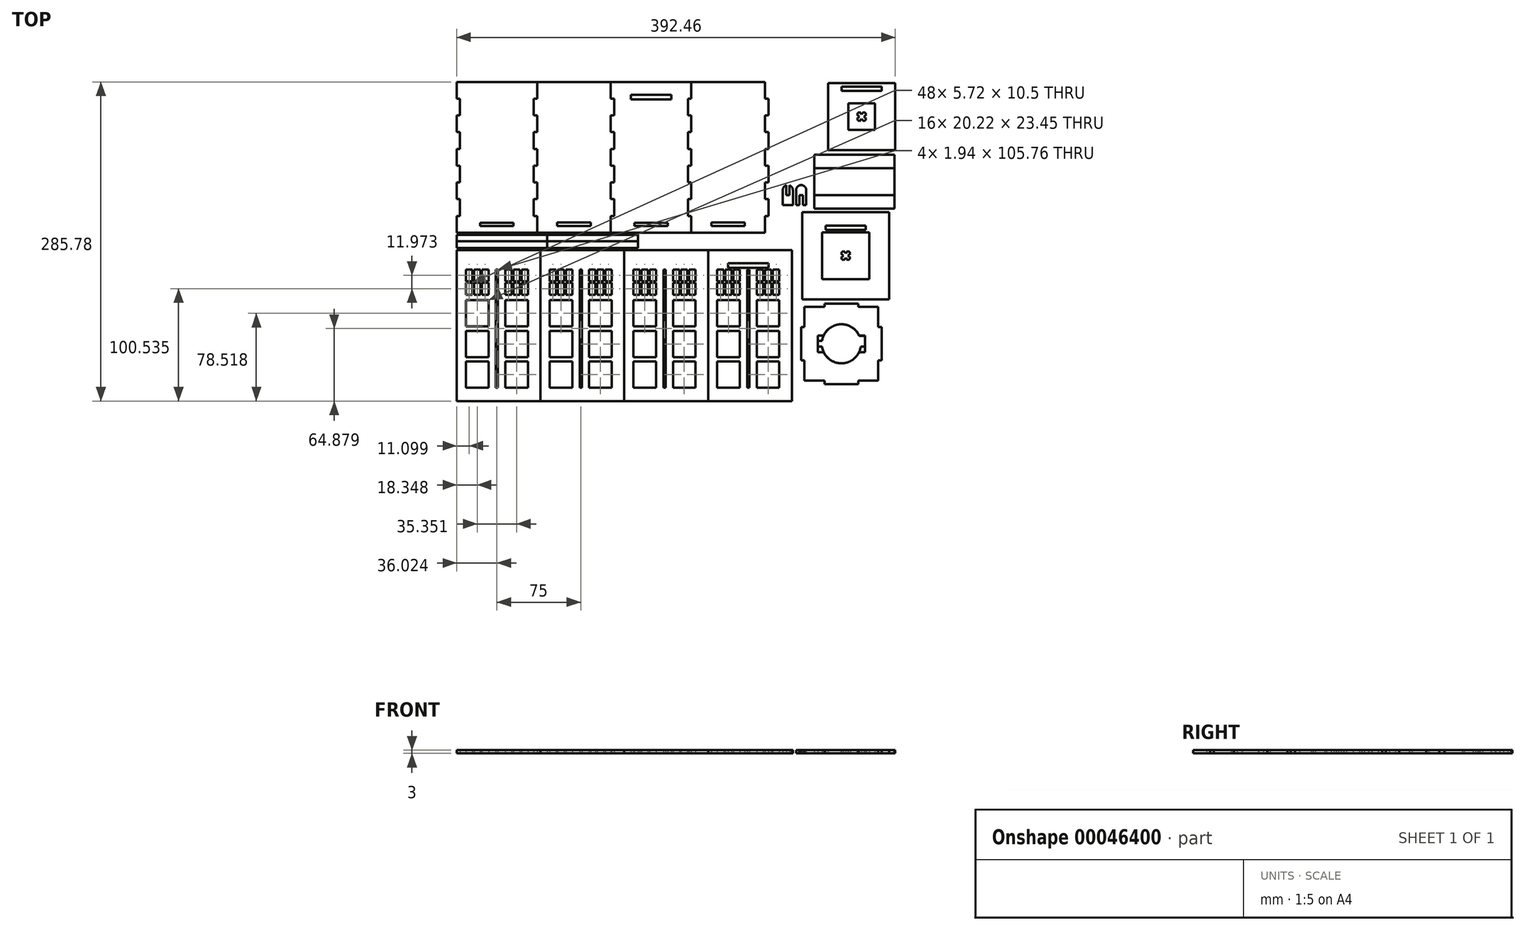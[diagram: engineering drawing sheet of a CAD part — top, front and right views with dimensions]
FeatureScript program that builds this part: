
annotation { "Feature Type Name" : "Feature", "Feature Type Description" : "" }
export const myFeature = defineFeature(function(context is Context, id is Id, definition is map)
    precondition{}
    {
        {
            var Q0;
            Q0=qCreatedBy(makeId("Top.planeOp"),FACE);
            var sketch = newSketch(context, id + "F0", { "sketchPlane" : qUnion([Q0])});
            skLineSegment(sketch, "E0", {"start": v(-210, -148.5) * mm, "end": v(210, -148.5) * mm});
            skLineSegment(sketch, "E1", {"start": v(210, -148.5) * mm, "end": v(210, 148.5) * mm});
            skLineSegment(sketch, "E2", {"start": v(210, 148.5) * mm, "end": v(-210, 148.5) * mm});
            skLineSegment(sketch, "E3", {"start": v(-210, 148.5) * mm, "end": v(-210, -148.5) * mm});
            skArc(sketch, "E4", {"start": v(115.56, 74.24) * mm, "mid": v(115.23, 70.83) * mm, "end": v(114.23, 67.54) * mm});
            skArc(sketch, "E5", {"start": v(114.23, 67.54) * mm, "mid": v(111.59, 63.14) * mm, "end": v(107.78, 59.7) * mm});
            skArc(sketch, "E6", {"start": v(107.78, 59.7) * mm, "mid": v(103.14, 57.5) * mm, "end": v(98.06, 56.74) * mm});
            skArc(sketch, "E7", {"start": v(98.06, 56.74) * mm, "mid": v(94.64, 57.08) * mm, "end": v(91.36, 58.07) * mm});
            skArc(sketch, "E8", {"start": v(91.36, 58.07) * mm, "mid": v(86.96, 60.71) * mm, "end": v(83.5, 64.52) * mm});
            skArc(sketch, "E9", {"start": v(83.5, 64.52) * mm, "mid": v(81.3, 69.16) * mm, "end": v(80.56, 74.24) * mm});
            skArc(sketch, "E10", {"start": v(80.56, 74.24) * mm, "mid": v(80.9, 77.66) * mm, "end": v(81.89, 80.94) * mm});
            skArc(sketch, "E11", {"start": v(81.89, 80.94) * mm, "mid": v(84.53, 85.34) * mm, "end": v(88.33, 88.8) * mm});
            skArc(sketch, "E12", {"start": v(88.33, 88.8) * mm, "mid": v(92.98, 91) * mm, "end": v(98.06, 91.74) * mm});
            skArc(sketch, "E13", {"start": v(98.06, 91.74) * mm, "mid": v(101.47, 91.4) * mm, "end": v(104.76, 90.41) * mm});
            skArc(sketch, "E14", {"start": v(104.76, 90.41) * mm, "mid": v(109.16, 87.77) * mm, "end": v(112.61, 83.97) * mm});
            skArc(sketch, "E15", {"start": v(112.61, 83.97) * mm, "mid": v(114.8, 79.32) * mm, "end": v(115.56, 74.24) * mm});
            skArc(sketch, "E16", {"start": v(127.35, 117.12) * mm, "mid": v(127.24, 114.87) * mm, "end": v(126.92, 112.64) * mm});
            skArc(sketch, "E17", {"start": v(126.92, 112.64) * mm, "mid": v(125.82, 108.84) * mm, "end": v(124.08, 105.3) * mm});
            skArc(sketch, "E18", {"start": v(124.08, 105.3) * mm, "mid": v(120.42, 100.66) * mm, "end": v(115.7, 97.1) * mm});
            skArc(sketch, "E19", {"start": v(115.7, 97.1) * mm, "mid": v(110.22, 94.88) * mm, "end": v(104.35, 94.13) * mm});
            skArc(sketch, "E20", {"start": v(104.35, 94.13) * mm, "mid": v(99.87, 94.56) * mm, "end": v(95.55, 95.87) * mm});
            skArc(sketch, "E21", {"start": v(95.55, 95.87) * mm, "mid": v(92.53, 97.4) * mm, "end": v(89.76, 99.34) * mm});
            skArc(sketch, "E22", {"start": v(89.76, 99.34) * mm, "mid": v(86.22, 102.97) * mm, "end": v(83.56, 107.29) * mm});
            skArc(sketch, "E23", {"start": v(83.56, 107.29) * mm, "mid": v(81.9, 112.08) * mm, "end": v(81.35, 117.12) * mm});
            skArc(sketch, "E24", {"start": v(81.35, 117.12) * mm, "mid": v(81.8, 121.61) * mm, "end": v(83.1, 125.93) * mm});
            skArc(sketch, "E25", {"start": v(83.1, 125.93) * mm, "mid": v(86.57, 131.72) * mm, "end": v(91.57, 136.25) * mm});
            skArc(sketch, "E26", {"start": v(91.57, 136.25) * mm, "mid": v(97.67, 139.14) * mm, "end": v(104.35, 140.12) * mm});
            skArc(sketch, "E27", {"start": v(104.35, 140.12) * mm, "mid": v(106.6, 140.02) * mm, "end": v(108.84, 139.69) * mm});
            skArc(sketch, "E28", {"start": v(108.84, 139.69) * mm, "mid": v(112.63, 138.59) * mm, "end": v(116.18, 136.86) * mm});
            skArc(sketch, "E29", {"start": v(116.18, 136.86) * mm, "mid": v(120.82, 133.19) * mm, "end": v(124.37, 128.46) * mm});
            skArc(sketch, "E30", {"start": v(124.37, 128.46) * mm, "mid": v(126.6, 122.99) * mm, "end": v(127.35, 117.12) * mm});
            skLineSegment(sketch, "E31", {"start": v(175.63, -78.56) * mm, "end": v(175.63, -60.56) * mm});
            skLineSegment(sketch, "E32", {"start": v(175.63, -60.56) * mm, "end": v(157.63, -60.56) * mm});
            skLineSegment(sketch, "E33", {"start": v(157.63, -60.56) * mm, "end": v(157.63, -57.56) * mm});
            skLineSegment(sketch, "E34", {"start": v(157.63, -57.56) * mm, "end": v(127.63, -57.56) * mm});
            skLineSegment(sketch, "E35", {"start": v(127.63, -57.56) * mm, "end": v(127.63, -60.56) * mm});
            skLineSegment(sketch, "E36", {"start": v(127.63, -60.56) * mm, "end": v(109.63, -60.56) * mm});
            skLineSegment(sketch, "E37", {"start": v(109.63, -60.56) * mm, "end": v(109.63, -78.56) * mm});
            skLineSegment(sketch, "E38", {"start": v(109.63, -78.56) * mm, "end": v(106.63, -78.56) * mm});
            skLineSegment(sketch, "E39", {"start": v(106.63, -78.56) * mm, "end": v(106.63, -108.56) * mm});
            skLineSegment(sketch, "E40", {"start": v(106.63, -108.56) * mm, "end": v(109.63, -108.56) * mm});
            skLineSegment(sketch, "E41", {"start": v(109.63, -108.56) * mm, "end": v(109.63, -126.56) * mm});
            skLineSegment(sketch, "E42", {"start": v(109.63, -126.56) * mm, "end": v(127.63, -126.56) * mm});
            skLineSegment(sketch, "E43", {"start": v(127.63, -126.56) * mm, "end": v(127.63, -129.56) * mm});
            skLineSegment(sketch, "E44", {"start": v(127.63, -129.56) * mm, "end": v(157.63, -129.56) * mm});
            skLineSegment(sketch, "E45", {"start": v(157.63, -129.56) * mm, "end": v(157.63, -126.56) * mm});
            skLineSegment(sketch, "E46", {"start": v(157.63, -126.56) * mm, "end": v(175.63, -126.56) * mm});
            skLineSegment(sketch, "E47", {"start": v(175.63, -126.56) * mm, "end": v(175.63, -108.56) * mm});
            skLineSegment(sketch, "E48", {"start": v(175.63, -108.56) * mm, "end": v(178.63, -108.56) * mm});
            skLineSegment(sketch, "E49", {"start": v(178.63, -108.56) * mm, "end": v(178.63, -78.56) * mm});
            skLineSegment(sketch, "E50", {"start": v(178.63, -78.56) * mm, "end": v(175.63, -78.56) * mm});
            skLineSegment(sketch, "E51", {"start": v(96.13, 48.35) * mm, "end": v(96.13, 39.6) * mm});
            skLineSegment(sketch, "E52", {"start": v(96.13, 39.6) * mm, "end": v(93.17, 39.6) * mm});
            skLineSegment(sketch, "E53", {"start": v(93.17, 39.6) * mm, "end": v(93.17, 48.33) * mm});
            skArc(sketch, "E54", {"start": v(93.17, 48.33) * mm, "mid": v(91.96, 47.68) * mm, "end": v(91, 46.7) * mm});
            skArc(sketch, "E55", {"start": v(91, 46.7) * mm, "mid": v(90.38, 45.46) * mm, "end": v(90.17, 44.1) * mm});
            skLineSegment(sketch, "E56", {"start": v(90.17, 44.1) * mm, "end": v(90.17, 30.6) * mm});
            skLineSegment(sketch, "E57", {"start": v(90.17, 30.6) * mm, "end": v(99.17, 30.6) * mm});
            skLineSegment(sketch, "E58", {"start": v(99.17, 30.6) * mm, "end": v(99.17, 44.1) * mm});
            skArc(sketch, "E59", {"start": v(99.17, 44.1) * mm, "mid": v(98.96, 45.47) * mm, "end": v(98.33, 46.7) * mm});
            skArc(sketch, "E60", {"start": v(98.33, 46.7) * mm, "mid": v(97.36, 47.7) * mm, "end": v(96.13, 48.35) * mm});
            skArc(sketch, "E61", {"start": v(106.63, 48.6) * mm, "mid": v(104.91, 48.25) * mm, "end": v(103.45, 47.28) * mm});
            skArc(sketch, "E62", {"start": v(103.45, 47.28) * mm, "mid": v(102.47, 45.82) * mm, "end": v(102.13, 44.1) * mm});
            skLineSegment(sketch, "E63", {"start": v(102.13, 44.1) * mm, "end": v(102.13, 30.6) * mm});
            skLineSegment(sketch, "E64", {"start": v(102.13, 30.6) * mm, "end": v(105.13, 30.6) * mm});
            skLineSegment(sketch, "E65", {"start": v(105.13, 30.6) * mm, "end": v(105.13, 39.6) * mm});
            skLineSegment(sketch, "E66", {"start": v(105.13, 39.6) * mm, "end": v(108.13, 39.6) * mm});
            skLineSegment(sketch, "E67", {"start": v(108.13, 39.6) * mm, "end": v(108.13, 30.6) * mm});
            skLineSegment(sketch, "E68", {"start": v(108.13, 30.6) * mm, "end": v(111.13, 30.6) * mm});
            skLineSegment(sketch, "E69", {"start": v(111.13, 30.6) * mm, "end": v(111.13, 44.1) * mm});
            skArc(sketch, "E70", {"start": v(111.13, 44.1) * mm, "mid": v(110.8, 45.82) * mm, "end": v(109.82, 47.28) * mm});
            skArc(sketch, "E71", {"start": v(109.82, 47.28) * mm, "mid": v(108.36, 48.25) * mm, "end": v(106.63, 48.6) * mm});
            skLineSegment(sketch, "E72", {"start": v(118.32, 63.57) * mm, "end": v(118.32, 75.57) * mm});
            skLineSegment(sketch, "E73", {"start": v(118.32, 75.57) * mm, "end": v(190.28, 75.57) * mm});
            skLineSegment(sketch, "E74", {"start": v(190.28, 75.57) * mm, "end": v(190.28, 63.57) * mm});
            skLineSegment(sketch, "E75", {"start": v(118.32, 51.57) * mm, "end": v(118.32, 63.57) * mm});
            skLineSegment(sketch, "E76", {"start": v(118.32, 63.57) * mm, "end": v(190.28, 63.57) * mm});
            skLineSegment(sketch, "E77", {"start": v(190.28, 63.57) * mm, "end": v(190.28, 51.57) * mm});
            skLineSegment(sketch, "E78", {"start": v(118.32, 39.57) * mm, "end": v(118.32, 51.57) * mm});
            skLineSegment(sketch, "E79", {"start": v(118.32, 51.57) * mm, "end": v(190.28, 51.57) * mm});
            skLineSegment(sketch, "E80", {"start": v(190.28, 51.57) * mm, "end": v(190.28, 39.57) * mm});
            skLineSegment(sketch, "E81", {"start": v(118.32, 27.57) * mm, "end": v(118.32, 39.57) * mm});
            skLineSegment(sketch, "E82", {"start": v(118.32, 39.57) * mm, "end": v(190.28, 39.57) * mm});
            skLineSegment(sketch, "E83", {"start": v(190.28, 39.57) * mm, "end": v(190.28, 27.57) * mm});
            skLineSegment(sketch, "E84", {"start": v(190.28, 27.57) * mm, "end": v(118.32, 27.57) * mm});
            skLineSegment(sketch, "E85", {"start": v(185.47, -53.68) * mm, "end": v(107.47, -53.68) * mm});
            skLineSegment(sketch, "E86", {"start": v(107.47, -53.68) * mm, "end": v(107.47, 24.32) * mm});
            skLineSegment(sketch, "E87", {"start": v(107.47, 24.32) * mm, "end": v(185.47, 24.32) * mm});
            skLineSegment(sketch, "E88", {"start": v(185.47, 24.32) * mm, "end": v(185.47, -53.68) * mm});
            skLineSegment(sketch, "E89", {"start": v(-126.69, -9.83) * mm, "end": v(-201.69, -9.83) * mm});
            skLineSegment(sketch, "E90", {"start": v(-201.69, -9.83) * mm, "end": v(-201.69, -144.83) * mm});
            skLineSegment(sketch, "E91", {"start": v(-201.69, -144.83) * mm, "end": v(-126.69, -144.83) * mm});
            skLineSegment(sketch, "E92", {"start": v(-126.69, -144.83) * mm, "end": v(-126.69, -9.83) * mm});
            skLineSegment(sketch, "E93", {"start": v(-126.69, -144.83) * mm, "end": v(-51.69, -144.83) * mm});
            skLineSegment(sketch, "E94", {"start": v(-51.69, -144.83) * mm, "end": v(-51.69, -144.83) * mm});
            skLineSegment(sketch, "E95", {"start": v(-51.69, -144.83) * mm, "end": v(-51.69, -9.83) * mm});
            skLineSegment(sketch, "E96", {"start": v(-51.69, -9.83) * mm, "end": v(-51.69, -9.83) * mm});
            skLineSegment(sketch, "E97", {"start": v(-51.69, -9.83) * mm, "end": v(-126.69, -9.83) * mm});
            skLineSegment(sketch, "E98", {"start": v(-51.69, -144.83) * mm, "end": v(23.31, -144.83) * mm});
            skLineSegment(sketch, "E99", {"start": v(23.31, -144.83) * mm, "end": v(23.31, -9.83) * mm});
            skLineSegment(sketch, "E100", {"start": v(23.31, -9.83) * mm, "end": v(-51.69, -9.83) * mm});
            skLineSegment(sketch, "E101", {"start": v(23.31, -144.83) * mm, "end": v(98.31, -144.83) * mm});
            skLineSegment(sketch, "E102", {"start": v(98.31, -144.83) * mm, "end": v(98.31, -9.83) * mm});
            skLineSegment(sketch, "E103", {"start": v(98.31, -9.83) * mm, "end": v(23.31, -9.83) * mm});
            skLineSegment(sketch, "E104", {"start": v(190.75, 79.8) * mm, "end": v(130.75, 79.8) * mm});
            skLineSegment(sketch, "E105", {"start": v(130.75, 79.8) * mm, "end": v(130.75, 139.8) * mm});
            skLineSegment(sketch, "E106", {"start": v(130.75, 139.8) * mm, "end": v(190.75, 139.8) * mm});
            skLineSegment(sketch, "E107", {"start": v(190.75, 139.8) * mm, "end": v(190.75, 79.8) * mm});
            skLineSegment(sketch, "E108", {"start": v(-39.56, -7.73) * mm, "end": v(-39.56, -1.8) * mm});
            skLineSegment(sketch, "E109", {"start": v(-39.56, -1.8) * mm, "end": v(-39.56, 4.12) * mm});
            skLineSegment(sketch, "E110", {"start": v(-39.56, 4.12) * mm, "end": v(-120.56, 4.12) * mm});
            skLineSegment(sketch, "E111", {"start": v(-120.56, 4.12) * mm, "end": v(-201.56, 4.12) * mm});
            skLineSegment(sketch, "E112", {"start": v(-201.56, 4.12) * mm, "end": v(-201.56, -1.8) * mm});
            skLineSegment(sketch, "E113", {"start": v(-201.56, -1.8) * mm, "end": v(-201.56, -7.73) * mm});
            skLineSegment(sketch, "E114", {"start": v(-201.56, -7.73) * mm, "end": v(-120.56, -7.73) * mm});
            skLineSegment(sketch, "E115", {"start": v(-120.56, -7.73) * mm, "end": v(-39.56, -7.73) * mm});
            skLineSegment(sketch, "E116", {"start": v(74.29, 5.95) * mm, "end": v(74.29, 20.95) * mm});
            skLineSegment(sketch, "E117", {"start": v(74.29, 20.95) * mm, "end": v(77.29, 20.95) * mm});
            skLineSegment(sketch, "E118", {"start": v(77.29, 20.95) * mm, "end": v(77.29, 35.95) * mm});
            skLineSegment(sketch, "E119", {"start": v(77.29, 35.95) * mm, "end": v(74.29, 35.95) * mm});
            skLineSegment(sketch, "E120", {"start": v(74.29, 35.95) * mm, "end": v(74.29, 50.95) * mm});
            skLineSegment(sketch, "E121", {"start": v(74.29, 50.95) * mm, "end": v(77.29, 50.95) * mm});
            skLineSegment(sketch, "E122", {"start": v(77.29, 50.95) * mm, "end": v(77.29, 65.95) * mm});
            skLineSegment(sketch, "E123", {"start": v(77.29, 65.95) * mm, "end": v(74.29, 65.95) * mm});
            skLineSegment(sketch, "E124", {"start": v(74.29, 65.95) * mm, "end": v(74.29, 80.95) * mm});
            skLineSegment(sketch, "E125", {"start": v(74.29, 80.95) * mm, "end": v(77.29, 80.95) * mm});
            skLineSegment(sketch, "E126", {"start": v(77.29, 80.95) * mm, "end": v(77.29, 95.95) * mm});
            skLineSegment(sketch, "E127", {"start": v(77.29, 95.95) * mm, "end": v(74.29, 95.95) * mm});
            skLineSegment(sketch, "E128", {"start": v(74.29, 95.95) * mm, "end": v(74.29, 110.95) * mm});
            skLineSegment(sketch, "E129", {"start": v(74.29, 110.95) * mm, "end": v(77.29, 110.95) * mm});
            skLineSegment(sketch, "E130", {"start": v(77.29, 110.95) * mm, "end": v(77.29, 125.95) * mm});
            skLineSegment(sketch, "E131", {"start": v(77.29, 125.95) * mm, "end": v(74.29, 125.95) * mm});
            skLineSegment(sketch, "E132", {"start": v(74.29, 125.95) * mm, "end": v(74.29, 140.95) * mm});
            skLineSegment(sketch, "E133", {"start": v(74.29, 140.95) * mm, "end": v(-201.71, 140.95) * mm});
            skLineSegment(sketch, "E134", {"start": v(-201.71, 140.95) * mm, "end": v(-201.71, 125.95) * mm});
            skLineSegment(sketch, "E135", {"start": v(-201.71, 125.95) * mm, "end": v(-198.71, 125.95) * mm});
            skLineSegment(sketch, "E136", {"start": v(-198.71, 125.95) * mm, "end": v(-198.71, 110.95) * mm});
            skLineSegment(sketch, "E137", {"start": v(-198.71, 110.95) * mm, "end": v(-201.71, 110.95) * mm});
            skLineSegment(sketch, "E138", {"start": v(-201.71, 110.95) * mm, "end": v(-201.71, 95.95) * mm});
            skLineSegment(sketch, "E139", {"start": v(-201.71, 95.95) * mm, "end": v(-198.71, 95.95) * mm});
            skLineSegment(sketch, "E140", {"start": v(-198.71, 95.95) * mm, "end": v(-198.71, 80.95) * mm});
            skLineSegment(sketch, "E141", {"start": v(-198.71, 80.95) * mm, "end": v(-201.71, 80.95) * mm});
            skLineSegment(sketch, "E142", {"start": v(-201.71, 80.95) * mm, "end": v(-201.71, 65.95) * mm});
            skLineSegment(sketch, "E143", {"start": v(-201.71, 65.95) * mm, "end": v(-198.71, 65.95) * mm});
            skLineSegment(sketch, "E144", {"start": v(-198.71, 65.95) * mm, "end": v(-198.71, 50.95) * mm});
            skLineSegment(sketch, "E145", {"start": v(-198.71, 50.95) * mm, "end": v(-201.71, 50.95) * mm});
            skLineSegment(sketch, "E146", {"start": v(-201.71, 50.95) * mm, "end": v(-201.71, 35.95) * mm});
            skLineSegment(sketch, "E147", {"start": v(-201.71, 35.95) * mm, "end": v(-198.71, 35.95) * mm});
            skLineSegment(sketch, "E148", {"start": v(-198.71, 35.95) * mm, "end": v(-198.71, 20.95) * mm});
            skLineSegment(sketch, "E149", {"start": v(-198.71, 20.95) * mm, "end": v(-201.71, 20.95) * mm});
            skLineSegment(sketch, "E150", {"start": v(-201.71, 20.95) * mm, "end": v(-201.71, 5.95) * mm});
            skLineSegment(sketch, "E151", {"start": v(-201.71, 5.95) * mm, "end": v(74.29, 5.95) * mm});
            skLineSegment(sketch, "E152", {"start": v(-180.71, 11.95) * mm, "end": v(-180.71, 14.68) * mm});
            skLineSegment(sketch, "E153", {"start": v(-180.71, 14.68) * mm, "end": v(-150.71, 14.68) * mm});
            skLineSegment(sketch, "E154", {"start": v(-150.71, 14.68) * mm, "end": v(-150.71, 11.95) * mm});
            skLineSegment(sketch, "E155", {"start": v(-150.71, 11.95) * mm, "end": v(-180.71, 11.95) * mm});
            skLineSegment(sketch, "E156", {"start": v(-111.71, 11.95) * mm, "end": v(-111.71, 14.95) * mm});
            skLineSegment(sketch, "E157", {"start": v(-111.71, 14.95) * mm, "end": v(-81.71, 14.95) * mm});
            skLineSegment(sketch, "E158", {"start": v(-81.71, 14.95) * mm, "end": v(-81.71, 11.95) * mm});
            skLineSegment(sketch, "E159", {"start": v(-81.71, 11.95) * mm, "end": v(-111.71, 11.95) * mm});
            skLineSegment(sketch, "E160", {"start": v(-42.71, 11.95) * mm, "end": v(-42.71, 14.68) * mm});
            skLineSegment(sketch, "E161", {"start": v(-42.71, 14.68) * mm, "end": v(-12.71, 14.68) * mm});
            skLineSegment(sketch, "E162", {"start": v(-12.71, 14.68) * mm, "end": v(-12.71, 11.95) * mm});
            skLineSegment(sketch, "E163", {"start": v(-12.71, 11.95) * mm, "end": v(-42.71, 11.95) * mm});
            skLineSegment(sketch, "E164", {"start": v(26.29, 11.95) * mm, "end": v(26.29, 14.95) * mm});
            skLineSegment(sketch, "E165", {"start": v(26.29, 14.95) * mm, "end": v(56.29, 14.95) * mm});
            skLineSegment(sketch, "E166", {"start": v(56.29, 14.95) * mm, "end": v(56.29, 11.95) * mm});
            skLineSegment(sketch, "E167", {"start": v(56.29, 11.95) * mm, "end": v(26.29, 11.95) * mm});
            skLineSegment(sketch, "E168", {"start": v(-9.71, 125.3) * mm, "end": v(-45.71, 125.3) * mm});
            skLineSegment(sketch, "E169", {"start": v(-45.71, 125.3) * mm, "end": v(-45.71, 129.3) * mm});
            skLineSegment(sketch, "E170", {"start": v(-45.71, 129.3) * mm, "end": v(-9.71, 129.3) * mm});
            skLineSegment(sketch, "E171", {"start": v(-9.71, 129.3) * mm, "end": v(-9.71, 125.3) * mm});
            skLineSegment(sketch, "E172", {"start": v(-37.75, -37.57) * mm, "end": v(-43.47, -37.57) * mm});
            skLineSegment(sketch, "E173", {"start": v(-43.47, -37.57) * mm, "end": v(-43.47, -27.07) * mm});
            skLineSegment(sketch, "E174", {"start": v(-43.47, -27.07) * mm, "end": v(-37.75, -27.07) * mm});
            skLineSegment(sketch, "E175", {"start": v(-37.75, -27.07) * mm, "end": v(-37.75, -37.57) * mm});
            skLineSegment(sketch, "E176", {"start": v(-30.5, -37.57) * mm, "end": v(-36.22, -37.57) * mm});
            skLineSegment(sketch, "E177", {"start": v(-36.22, -37.57) * mm, "end": v(-36.22, -27.07) * mm});
            skLineSegment(sketch, "E178", {"start": v(-36.22, -27.07) * mm, "end": v(-30.5, -27.07) * mm});
            skLineSegment(sketch, "E179", {"start": v(-30.5, -27.07) * mm, "end": v(-30.5, -37.57) * mm});
            skLineSegment(sketch, "E180", {"start": v(-23.26, -37.57) * mm, "end": v(-28.97, -37.57) * mm});
            skLineSegment(sketch, "E181", {"start": v(-28.97, -37.57) * mm, "end": v(-28.97, -27.07) * mm});
            skLineSegment(sketch, "E182", {"start": v(-28.97, -27.07) * mm, "end": v(-23.26, -27.07) * mm});
            skLineSegment(sketch, "E183", {"start": v(-23.26, -27.07) * mm, "end": v(-23.26, -37.57) * mm});
            skLineSegment(sketch, "E184", {"start": v(-37.75, -49.55) * mm, "end": v(-43.47, -49.55) * mm});
            skLineSegment(sketch, "E185", {"start": v(-43.47, -49.55) * mm, "end": v(-43.47, -39.04) * mm});
            skLineSegment(sketch, "E186", {"start": v(-43.47, -39.04) * mm, "end": v(-37.75, -39.04) * mm});
            skLineSegment(sketch, "E187", {"start": v(-37.75, -39.04) * mm, "end": v(-37.75, -49.55) * mm});
            skLineSegment(sketch, "E188", {"start": v(-30.5, -49.55) * mm, "end": v(-36.22, -49.55) * mm});
            skLineSegment(sketch, "E189", {"start": v(-36.22, -49.55) * mm, "end": v(-36.22, -39.04) * mm});
            skLineSegment(sketch, "E190", {"start": v(-36.22, -39.04) * mm, "end": v(-30.5, -39.04) * mm});
            skLineSegment(sketch, "E191", {"start": v(-30.5, -39.04) * mm, "end": v(-30.5, -49.55) * mm});
            skLineSegment(sketch, "E192", {"start": v(-23.26, -49.55) * mm, "end": v(-28.97, -49.55) * mm});
            skLineSegment(sketch, "E193", {"start": v(-28.97, -49.55) * mm, "end": v(-28.97, -39.04) * mm});
            skLineSegment(sketch, "E194", {"start": v(-28.97, -39.04) * mm, "end": v(-23.26, -39.04) * mm});
            skLineSegment(sketch, "E195", {"start": v(-23.26, -39.04) * mm, "end": v(-23.26, -49.55) * mm});
            skLineSegment(sketch, "E196", {"start": v(-23.26, -105.44) * mm, "end": v(-43.47, -105.44) * mm});
            skLineSegment(sketch, "E197", {"start": v(-43.47, -105.44) * mm, "end": v(-43.47, -81.98) * mm});
            skLineSegment(sketch, "E198", {"start": v(-43.47, -81.98) * mm, "end": v(-23.26, -81.98) * mm});
            skLineSegment(sketch, "E199", {"start": v(-23.26, -81.98) * mm, "end": v(-23.26, -105.44) * mm});
            skLineSegment(sketch, "E200", {"start": v(-23.26, -132.83) * mm, "end": v(-43.47, -132.83) * mm});
            skLineSegment(sketch, "E201", {"start": v(-43.47, -132.83) * mm, "end": v(-43.47, -109.38) * mm});
            skLineSegment(sketch, "E202", {"start": v(-43.47, -109.38) * mm, "end": v(-23.26, -109.38) * mm});
            skLineSegment(sketch, "E203", {"start": v(-23.26, -109.38) * mm, "end": v(-23.26, -132.83) * mm});
            skLineSegment(sketch, "E204", {"start": v(6.38, -37.57) * mm, "end": v(12.1, -37.57) * mm});
            skLineSegment(sketch, "E205", {"start": v(12.1, -37.57) * mm, "end": v(12.1, -27.07) * mm});
            skLineSegment(sketch, "E206", {"start": v(12.1, -27.07) * mm, "end": v(6.38, -27.07) * mm});
            skLineSegment(sketch, "E207", {"start": v(6.38, -27.07) * mm, "end": v(6.38, -37.57) * mm});
            skLineSegment(sketch, "E208", {"start": v(-0.87, -37.57) * mm, "end": v(4.85, -37.57) * mm});
            skLineSegment(sketch, "E209", {"start": v(4.85, -37.57) * mm, "end": v(4.85, -27.07) * mm});
            skLineSegment(sketch, "E210", {"start": v(4.85, -27.07) * mm, "end": v(-0.87, -27.07) * mm});
            skLineSegment(sketch, "E211", {"start": v(-0.87, -27.07) * mm, "end": v(-0.87, -37.57) * mm});
            skLineSegment(sketch, "E212", {"start": v(-8.12, -37.57) * mm, "end": v(-2.4, -37.57) * mm});
            skLineSegment(sketch, "E213", {"start": v(-2.4, -37.57) * mm, "end": v(-2.4, -27.07) * mm});
            skLineSegment(sketch, "E214", {"start": v(-2.4, -27.07) * mm, "end": v(-8.12, -27.07) * mm});
            skLineSegment(sketch, "E215", {"start": v(-8.12, -27.07) * mm, "end": v(-8.12, -37.57) * mm});
            skLineSegment(sketch, "E216", {"start": v(6.38, -49.55) * mm, "end": v(12.1, -49.55) * mm});
            skLineSegment(sketch, "E217", {"start": v(12.1, -49.55) * mm, "end": v(12.1, -39.04) * mm});
            skLineSegment(sketch, "E218", {"start": v(12.1, -39.04) * mm, "end": v(6.38, -39.04) * mm});
            skLineSegment(sketch, "E219", {"start": v(6.38, -39.04) * mm, "end": v(6.38, -49.55) * mm});
            skLineSegment(sketch, "E220", {"start": v(-0.87, -49.55) * mm, "end": v(4.85, -49.55) * mm});
            skLineSegment(sketch, "E221", {"start": v(4.85, -49.55) * mm, "end": v(4.85, -39.04) * mm});
            skLineSegment(sketch, "E222", {"start": v(4.85, -39.04) * mm, "end": v(-0.87, -39.04) * mm});
            skLineSegment(sketch, "E223", {"start": v(-0.87, -39.04) * mm, "end": v(-0.87, -49.55) * mm});
            skLineSegment(sketch, "E224", {"start": v(-8.12, -49.55) * mm, "end": v(-2.4, -49.55) * mm});
            skLineSegment(sketch, "E225", {"start": v(-2.4, -49.55) * mm, "end": v(-2.4, -39.04) * mm});
            skLineSegment(sketch, "E226", {"start": v(-2.4, -39.04) * mm, "end": v(-8.12, -39.04) * mm});
            skLineSegment(sketch, "E227", {"start": v(-8.12, -39.04) * mm, "end": v(-8.12, -49.55) * mm});
            skLineSegment(sketch, "E228", {"start": v(-8.12, -105.44) * mm, "end": v(12.1, -105.44) * mm});
            skLineSegment(sketch, "E229", {"start": v(12.1, -105.44) * mm, "end": v(12.1, -81.98) * mm});
            skLineSegment(sketch, "E230", {"start": v(12.1, -81.98) * mm, "end": v(-8.12, -81.98) * mm});
            skLineSegment(sketch, "E231", {"start": v(-8.12, -81.98) * mm, "end": v(-8.12, -105.44) * mm});
            skLineSegment(sketch, "E232", {"start": v(-8.12, -132.83) * mm, "end": v(12.1, -132.83) * mm});
            skLineSegment(sketch, "E233", {"start": v(12.1, -132.83) * mm, "end": v(12.1, -109.38) * mm});
            skLineSegment(sketch, "E234", {"start": v(12.1, -109.38) * mm, "end": v(-8.12, -109.38) * mm});
            skLineSegment(sketch, "E235", {"start": v(-8.12, -109.38) * mm, "end": v(-8.12, -132.83) * mm});
            skLineSegment(sketch, "E236", {"start": v(-8.12, -78.04) * mm, "end": v(12.1, -78.04) * mm});
            skLineSegment(sketch, "E237", {"start": v(12.1, -78.04) * mm, "end": v(12.1, -54.59) * mm});
            skLineSegment(sketch, "E238", {"start": v(12.1, -54.59) * mm, "end": v(-8.12, -54.59) * mm});
            skLineSegment(sketch, "E239", {"start": v(-8.12, -54.59) * mm, "end": v(-8.12, -78.04) * mm});
            skLineSegment(sketch, "E240", {"start": v(-14.71, -132.83) * mm, "end": v(-16.66, -132.83) * mm});
            skLineSegment(sketch, "E241", {"start": v(-16.66, -132.83) * mm, "end": v(-16.66, -27.07) * mm});
            skLineSegment(sketch, "E242", {"start": v(-16.66, -27.07) * mm, "end": v(-14.71, -27.07) * mm});
            skLineSegment(sketch, "E243", {"start": v(-14.71, -27.07) * mm, "end": v(-14.71, -132.83) * mm});
            skLineSegment(sketch, "E244", {"start": v(-43.47, -78.04) * mm, "end": v(-23.25, -78.04) * mm});
            skLineSegment(sketch, "E245", {"start": v(-23.25, -78.04) * mm, "end": v(-23.25, -54.59) * mm});
            skLineSegment(sketch, "E246", {"start": v(-23.25, -54.59) * mm, "end": v(-43.47, -54.59) * mm});
            skLineSegment(sketch, "E247", {"start": v(-43.47, -54.59) * mm, "end": v(-43.47, -78.04) * mm});
            skLineSegment(sketch, "E248", {"start": v(-187.75, -37.57) * mm, "end": v(-193.47, -37.57) * mm});
            skLineSegment(sketch, "E249", {"start": v(-193.47, -37.57) * mm, "end": v(-193.47, -27.07) * mm});
            skLineSegment(sketch, "E250", {"start": v(-193.47, -27.07) * mm, "end": v(-187.75, -27.07) * mm});
            skLineSegment(sketch, "E251", {"start": v(-187.75, -27.07) * mm, "end": v(-187.75, -37.57) * mm});
            skLineSegment(sketch, "E252", {"start": v(-180.5, -37.57) * mm, "end": v(-186.22, -37.57) * mm});
            skLineSegment(sketch, "E253", {"start": v(-186.22, -37.57) * mm, "end": v(-186.22, -27.07) * mm});
            skLineSegment(sketch, "E254", {"start": v(-186.22, -27.07) * mm, "end": v(-180.5, -27.07) * mm});
            skLineSegment(sketch, "E255", {"start": v(-180.5, -27.07) * mm, "end": v(-180.5, -37.57) * mm});
            skLineSegment(sketch, "E256", {"start": v(-173.26, -37.57) * mm, "end": v(-178.97, -37.57) * mm});
            skLineSegment(sketch, "E257", {"start": v(-178.97, -37.57) * mm, "end": v(-178.97, -27.07) * mm});
            skLineSegment(sketch, "E258", {"start": v(-178.97, -27.07) * mm, "end": v(-173.26, -27.07) * mm});
            skLineSegment(sketch, "E259", {"start": v(-173.26, -27.07) * mm, "end": v(-173.26, -37.57) * mm});
            skLineSegment(sketch, "E260", {"start": v(-187.75, -49.55) * mm, "end": v(-193.47, -49.55) * mm});
            skLineSegment(sketch, "E261", {"start": v(-193.47, -49.55) * mm, "end": v(-193.47, -39.04) * mm});
            skLineSegment(sketch, "E262", {"start": v(-193.47, -39.04) * mm, "end": v(-187.75, -39.04) * mm});
            skLineSegment(sketch, "E263", {"start": v(-187.75, -39.04) * mm, "end": v(-187.75, -49.55) * mm});
            skLineSegment(sketch, "E264", {"start": v(-180.5, -49.55) * mm, "end": v(-186.22, -49.55) * mm});
            skLineSegment(sketch, "E265", {"start": v(-186.22, -49.55) * mm, "end": v(-186.22, -39.04) * mm});
            skLineSegment(sketch, "E266", {"start": v(-186.22, -39.04) * mm, "end": v(-180.5, -39.04) * mm});
            skLineSegment(sketch, "E267", {"start": v(-180.5, -39.04) * mm, "end": v(-180.5, -49.55) * mm});
            skLineSegment(sketch, "E268", {"start": v(-173.26, -49.55) * mm, "end": v(-178.97, -49.55) * mm});
            skLineSegment(sketch, "E269", {"start": v(-178.97, -49.55) * mm, "end": v(-178.97, -39.04) * mm});
            skLineSegment(sketch, "E270", {"start": v(-178.97, -39.04) * mm, "end": v(-173.26, -39.04) * mm});
            skLineSegment(sketch, "E271", {"start": v(-173.26, -39.04) * mm, "end": v(-173.26, -49.55) * mm});
            skLineSegment(sketch, "E272", {"start": v(-173.26, -105.44) * mm, "end": v(-193.47, -105.44) * mm});
            skLineSegment(sketch, "E273", {"start": v(-193.47, -105.44) * mm, "end": v(-193.47, -81.98) * mm});
            skLineSegment(sketch, "E274", {"start": v(-193.47, -81.98) * mm, "end": v(-173.26, -81.98) * mm});
            skLineSegment(sketch, "E275", {"start": v(-173.26, -81.98) * mm, "end": v(-173.26, -105.44) * mm});
            skLineSegment(sketch, "E276", {"start": v(-173.26, -132.83) * mm, "end": v(-193.47, -132.83) * mm});
            skLineSegment(sketch, "E277", {"start": v(-193.47, -132.83) * mm, "end": v(-193.47, -109.38) * mm});
            skLineSegment(sketch, "E278", {"start": v(-193.47, -109.38) * mm, "end": v(-173.26, -109.38) * mm});
            skLineSegment(sketch, "E279", {"start": v(-173.26, -109.38) * mm, "end": v(-173.26, -132.83) * mm});
            skLineSegment(sketch, "E280", {"start": v(-143.62, -37.57) * mm, "end": v(-137.9, -37.57) * mm});
            skLineSegment(sketch, "E281", {"start": v(-137.9, -37.57) * mm, "end": v(-137.9, -27.07) * mm});
            skLineSegment(sketch, "E282", {"start": v(-137.9, -27.07) * mm, "end": v(-143.62, -27.07) * mm});
            skLineSegment(sketch, "E283", {"start": v(-143.62, -27.07) * mm, "end": v(-143.62, -37.57) * mm});
            skLineSegment(sketch, "E284", {"start": v(-150.87, -37.57) * mm, "end": v(-145.15, -37.57) * mm});
            skLineSegment(sketch, "E285", {"start": v(-145.15, -37.57) * mm, "end": v(-145.15, -27.07) * mm});
            skLineSegment(sketch, "E286", {"start": v(-145.15, -27.07) * mm, "end": v(-150.87, -27.07) * mm});
            skLineSegment(sketch, "E287", {"start": v(-150.87, -27.07) * mm, "end": v(-150.87, -37.57) * mm});
            skLineSegment(sketch, "E288", {"start": v(-158.12, -37.57) * mm, "end": v(-152.4, -37.57) * mm});
            skLineSegment(sketch, "E289", {"start": v(-152.4, -37.57) * mm, "end": v(-152.4, -27.07) * mm});
            skLineSegment(sketch, "E290", {"start": v(-152.4, -27.07) * mm, "end": v(-158.12, -27.07) * mm});
            skLineSegment(sketch, "E291", {"start": v(-158.12, -27.07) * mm, "end": v(-158.12, -37.57) * mm});
            skLineSegment(sketch, "E292", {"start": v(-143.62, -49.55) * mm, "end": v(-137.9, -49.55) * mm});
            skLineSegment(sketch, "E293", {"start": v(-137.9, -49.55) * mm, "end": v(-137.9, -39.04) * mm});
            skLineSegment(sketch, "E294", {"start": v(-137.9, -39.04) * mm, "end": v(-143.62, -39.04) * mm});
            skLineSegment(sketch, "E295", {"start": v(-143.62, -39.04) * mm, "end": v(-143.62, -49.55) * mm});
            skLineSegment(sketch, "E296", {"start": v(-150.87, -49.55) * mm, "end": v(-145.15, -49.55) * mm});
            skLineSegment(sketch, "E297", {"start": v(-145.15, -49.55) * mm, "end": v(-145.15, -39.04) * mm});
            skLineSegment(sketch, "E298", {"start": v(-145.15, -39.04) * mm, "end": v(-150.87, -39.04) * mm});
            skLineSegment(sketch, "E299", {"start": v(-150.87, -39.04) * mm, "end": v(-150.87, -49.55) * mm});
            skLineSegment(sketch, "E300", {"start": v(-158.12, -49.55) * mm, "end": v(-152.4, -49.55) * mm});
            skLineSegment(sketch, "E301", {"start": v(-152.4, -49.55) * mm, "end": v(-152.4, -39.04) * mm});
            skLineSegment(sketch, "E302", {"start": v(-152.4, -39.04) * mm, "end": v(-158.12, -39.04) * mm});
            skLineSegment(sketch, "E303", {"start": v(-158.12, -39.04) * mm, "end": v(-158.12, -49.55) * mm});
            skLineSegment(sketch, "E304", {"start": v(-158.12, -105.44) * mm, "end": v(-137.9, -105.44) * mm});
            skLineSegment(sketch, "E305", {"start": v(-137.9, -105.44) * mm, "end": v(-137.9, -81.98) * mm});
            skLineSegment(sketch, "E306", {"start": v(-137.9, -81.98) * mm, "end": v(-158.12, -81.98) * mm});
            skLineSegment(sketch, "E307", {"start": v(-158.12, -81.98) * mm, "end": v(-158.12, -105.44) * mm});
            skLineSegment(sketch, "E308", {"start": v(-158.12, -132.83) * mm, "end": v(-137.9, -132.83) * mm});
            skLineSegment(sketch, "E309", {"start": v(-137.9, -132.83) * mm, "end": v(-137.9, -109.38) * mm});
            skLineSegment(sketch, "E310", {"start": v(-137.9, -109.38) * mm, "end": v(-158.12, -109.38) * mm});
            skLineSegment(sketch, "E311", {"start": v(-158.12, -109.38) * mm, "end": v(-158.12, -132.83) * mm});
            skLineSegment(sketch, "E312", {"start": v(-158.12, -78.04) * mm, "end": v(-137.9, -78.04) * mm});
            skLineSegment(sketch, "E313", {"start": v(-137.9, -78.04) * mm, "end": v(-137.9, -54.59) * mm});
            skLineSegment(sketch, "E314", {"start": v(-137.9, -54.59) * mm, "end": v(-158.12, -54.59) * mm});
            skLineSegment(sketch, "E315", {"start": v(-158.12, -54.59) * mm, "end": v(-158.12, -78.04) * mm});
            skLineSegment(sketch, "E316", {"start": v(-164.71, -132.83) * mm, "end": v(-166.66, -132.83) * mm});
            skLineSegment(sketch, "E317", {"start": v(-166.66, -132.83) * mm, "end": v(-166.66, -27.07) * mm});
            skLineSegment(sketch, "E318", {"start": v(-166.66, -27.07) * mm, "end": v(-164.71, -27.07) * mm});
            skLineSegment(sketch, "E319", {"start": v(-164.71, -27.07) * mm, "end": v(-164.71, -132.83) * mm});
            skLineSegment(sketch, "E320", {"start": v(-193.47, -78.04) * mm, "end": v(-173.25, -78.04) * mm});
            skLineSegment(sketch, "E321", {"start": v(-173.25, -78.04) * mm, "end": v(-173.25, -54.59) * mm});
            skLineSegment(sketch, "E322", {"start": v(-173.25, -54.59) * mm, "end": v(-193.47, -54.59) * mm});
            skLineSegment(sketch, "E323", {"start": v(-193.47, -54.59) * mm, "end": v(-193.47, -78.04) * mm});
            skLineSegment(sketch, "E324", {"start": v(-112.75, -37.57) * mm, "end": v(-118.47, -37.57) * mm});
            skLineSegment(sketch, "E325", {"start": v(-118.47, -37.57) * mm, "end": v(-118.47, -27.07) * mm});
            skLineSegment(sketch, "E326", {"start": v(-118.47, -27.07) * mm, "end": v(-112.75, -27.07) * mm});
            skLineSegment(sketch, "E327", {"start": v(-112.75, -27.07) * mm, "end": v(-112.75, -37.57) * mm});
            skLineSegment(sketch, "E328", {"start": v(-105.5, -37.57) * mm, "end": v(-111.22, -37.57) * mm});
            skLineSegment(sketch, "E329", {"start": v(-111.22, -37.57) * mm, "end": v(-111.22, -27.07) * mm});
            skLineSegment(sketch, "E330", {"start": v(-111.22, -27.07) * mm, "end": v(-105.5, -27.07) * mm});
            skLineSegment(sketch, "E331", {"start": v(-105.5, -27.07) * mm, "end": v(-105.5, -37.57) * mm});
            skLineSegment(sketch, "E332", {"start": v(-98.26, -37.57) * mm, "end": v(-103.97, -37.57) * mm});
            skLineSegment(sketch, "E333", {"start": v(-103.97, -37.57) * mm, "end": v(-103.97, -27.07) * mm});
            skLineSegment(sketch, "E334", {"start": v(-103.97, -27.07) * mm, "end": v(-98.26, -27.07) * mm});
            skLineSegment(sketch, "E335", {"start": v(-98.26, -27.07) * mm, "end": v(-98.26, -37.57) * mm});
            skLineSegment(sketch, "E336", {"start": v(-112.75, -49.55) * mm, "end": v(-118.47, -49.55) * mm});
            skLineSegment(sketch, "E337", {"start": v(-118.47, -49.55) * mm, "end": v(-118.47, -39.04) * mm});
            skLineSegment(sketch, "E338", {"start": v(-118.47, -39.04) * mm, "end": v(-112.75, -39.04) * mm});
            skLineSegment(sketch, "E339", {"start": v(-112.75, -39.04) * mm, "end": v(-112.75, -49.55) * mm});
            skLineSegment(sketch, "E340", {"start": v(-105.5, -49.55) * mm, "end": v(-111.22, -49.55) * mm});
            skLineSegment(sketch, "E341", {"start": v(-111.22, -49.55) * mm, "end": v(-111.22, -39.04) * mm});
            skLineSegment(sketch, "E342", {"start": v(-111.22, -39.04) * mm, "end": v(-105.5, -39.04) * mm});
            skLineSegment(sketch, "E343", {"start": v(-105.5, -39.04) * mm, "end": v(-105.5, -49.55) * mm});
            skLineSegment(sketch, "E344", {"start": v(-98.26, -49.55) * mm, "end": v(-103.97, -49.55) * mm});
            skLineSegment(sketch, "E345", {"start": v(-103.97, -49.55) * mm, "end": v(-103.97, -39.04) * mm});
            skLineSegment(sketch, "E346", {"start": v(-103.97, -39.04) * mm, "end": v(-98.26, -39.04) * mm});
            skLineSegment(sketch, "E347", {"start": v(-98.26, -39.04) * mm, "end": v(-98.26, -49.55) * mm});
            skLineSegment(sketch, "E348", {"start": v(-98.26, -105.44) * mm, "end": v(-118.47, -105.44) * mm});
            skLineSegment(sketch, "E349", {"start": v(-118.47, -105.44) * mm, "end": v(-118.47, -81.98) * mm});
            skLineSegment(sketch, "E350", {"start": v(-118.47, -81.98) * mm, "end": v(-98.26, -81.98) * mm});
            skLineSegment(sketch, "E351", {"start": v(-98.26, -81.98) * mm, "end": v(-98.26, -105.44) * mm});
            skLineSegment(sketch, "E352", {"start": v(-98.26, -132.83) * mm, "end": v(-118.47, -132.83) * mm});
            skLineSegment(sketch, "E353", {"start": v(-118.47, -132.83) * mm, "end": v(-118.47, -109.38) * mm});
            skLineSegment(sketch, "E354", {"start": v(-118.47, -109.38) * mm, "end": v(-98.26, -109.38) * mm});
            skLineSegment(sketch, "E355", {"start": v(-98.26, -109.38) * mm, "end": v(-98.26, -132.83) * mm});
            skLineSegment(sketch, "E356", {"start": v(-68.62, -37.57) * mm, "end": v(-62.9, -37.57) * mm});
            skLineSegment(sketch, "E357", {"start": v(-62.9, -37.57) * mm, "end": v(-62.9, -27.07) * mm});
            skLineSegment(sketch, "E358", {"start": v(-62.9, -27.07) * mm, "end": v(-68.62, -27.07) * mm});
            skLineSegment(sketch, "E359", {"start": v(-68.62, -27.07) * mm, "end": v(-68.62, -37.57) * mm});
            skLineSegment(sketch, "E360", {"start": v(-75.87, -37.57) * mm, "end": v(-70.15, -37.57) * mm});
            skLineSegment(sketch, "E361", {"start": v(-70.15, -37.57) * mm, "end": v(-70.15, -27.07) * mm});
            skLineSegment(sketch, "E362", {"start": v(-70.15, -27.07) * mm, "end": v(-75.87, -27.07) * mm});
            skLineSegment(sketch, "E363", {"start": v(-75.87, -27.07) * mm, "end": v(-75.87, -37.57) * mm});
            skLineSegment(sketch, "E364", {"start": v(-83.12, -37.57) * mm, "end": v(-77.4, -37.57) * mm});
            skLineSegment(sketch, "E365", {"start": v(-77.4, -37.57) * mm, "end": v(-77.4, -27.07) * mm});
            skLineSegment(sketch, "E366", {"start": v(-77.4, -27.07) * mm, "end": v(-83.12, -27.07) * mm});
            skLineSegment(sketch, "E367", {"start": v(-83.12, -27.07) * mm, "end": v(-83.12, -37.57) * mm});
            skLineSegment(sketch, "E368", {"start": v(-68.62, -49.55) * mm, "end": v(-62.9, -49.55) * mm});
            skLineSegment(sketch, "E369", {"start": v(-62.9, -49.55) * mm, "end": v(-62.9, -39.04) * mm});
            skLineSegment(sketch, "E370", {"start": v(-62.9, -39.04) * mm, "end": v(-68.62, -39.04) * mm});
            skLineSegment(sketch, "E371", {"start": v(-68.62, -39.04) * mm, "end": v(-68.62, -49.55) * mm});
            skLineSegment(sketch, "E372", {"start": v(-75.87, -49.55) * mm, "end": v(-70.15, -49.55) * mm});
            skLineSegment(sketch, "E373", {"start": v(-70.15, -49.55) * mm, "end": v(-70.15, -39.04) * mm});
            skLineSegment(sketch, "E374", {"start": v(-70.15, -39.04) * mm, "end": v(-75.87, -39.04) * mm});
            skLineSegment(sketch, "E375", {"start": v(-75.87, -39.04) * mm, "end": v(-75.87, -49.55) * mm});
            skLineSegment(sketch, "E376", {"start": v(-83.12, -49.55) * mm, "end": v(-77.4, -49.55) * mm});
            skLineSegment(sketch, "E377", {"start": v(-77.4, -49.55) * mm, "end": v(-77.4, -39.04) * mm});
            skLineSegment(sketch, "E378", {"start": v(-77.4, -39.04) * mm, "end": v(-83.12, -39.04) * mm});
            skLineSegment(sketch, "E379", {"start": v(-83.12, -39.04) * mm, "end": v(-83.12, -49.55) * mm});
            skLineSegment(sketch, "E380", {"start": v(-83.12, -105.44) * mm, "end": v(-62.9, -105.44) * mm});
            skLineSegment(sketch, "E381", {"start": v(-62.9, -105.44) * mm, "end": v(-62.9, -81.98) * mm});
            skLineSegment(sketch, "E382", {"start": v(-62.9, -81.98) * mm, "end": v(-83.12, -81.98) * mm});
            skLineSegment(sketch, "E383", {"start": v(-83.12, -81.98) * mm, "end": v(-83.12, -105.44) * mm});
            skLineSegment(sketch, "E384", {"start": v(-83.12, -132.83) * mm, "end": v(-62.9, -132.83) * mm});
            skLineSegment(sketch, "E385", {"start": v(-62.9, -132.83) * mm, "end": v(-62.9, -109.38) * mm});
            skLineSegment(sketch, "E386", {"start": v(-62.9, -109.38) * mm, "end": v(-83.12, -109.38) * mm});
            skLineSegment(sketch, "E387", {"start": v(-83.12, -109.38) * mm, "end": v(-83.12, -132.83) * mm});
            skLineSegment(sketch, "E388", {"start": v(-83.12, -78.04) * mm, "end": v(-62.9, -78.04) * mm});
            skLineSegment(sketch, "E389", {"start": v(-62.9, -78.04) * mm, "end": v(-62.9, -54.59) * mm});
            skLineSegment(sketch, "E390", {"start": v(-62.9, -54.59) * mm, "end": v(-83.12, -54.59) * mm});
            skLineSegment(sketch, "E391", {"start": v(-83.12, -54.59) * mm, "end": v(-83.12, -78.04) * mm});
            skLineSegment(sketch, "E392", {"start": v(-89.71, -132.83) * mm, "end": v(-91.66, -132.83) * mm});
            skLineSegment(sketch, "E393", {"start": v(-91.66, -132.83) * mm, "end": v(-91.66, -27.07) * mm});
            skLineSegment(sketch, "E394", {"start": v(-91.66, -27.07) * mm, "end": v(-89.71, -27.07) * mm});
            skLineSegment(sketch, "E395", {"start": v(-89.71, -27.07) * mm, "end": v(-89.71, -132.83) * mm});
            skLineSegment(sketch, "E396", {"start": v(-118.47, -78.04) * mm, "end": v(-98.25, -78.04) * mm});
            skLineSegment(sketch, "E397", {"start": v(-98.25, -78.04) * mm, "end": v(-98.25, -54.59) * mm});
            skLineSegment(sketch, "E398", {"start": v(-98.25, -54.59) * mm, "end": v(-118.47, -54.59) * mm});
            skLineSegment(sketch, "E399", {"start": v(-118.47, -54.59) * mm, "end": v(-118.47, -78.04) * mm});
            skLineSegment(sketch, "E400", {"start": v(37.25, -37.57) * mm, "end": v(31.53, -37.57) * mm});
            skLineSegment(sketch, "E401", {"start": v(31.53, -37.57) * mm, "end": v(31.53, -27.07) * mm});
            skLineSegment(sketch, "E402", {"start": v(31.53, -27.07) * mm, "end": v(37.25, -27.07) * mm});
            skLineSegment(sketch, "E403", {"start": v(37.25, -27.07) * mm, "end": v(37.25, -37.57) * mm});
            skLineSegment(sketch, "E404", {"start": v(44.5, -37.57) * mm, "end": v(38.78, -37.57) * mm});
            skLineSegment(sketch, "E405", {"start": v(38.78, -37.57) * mm, "end": v(38.78, -27.07) * mm});
            skLineSegment(sketch, "E406", {"start": v(38.78, -27.07) * mm, "end": v(44.5, -27.07) * mm});
            skLineSegment(sketch, "E407", {"start": v(44.5, -27.07) * mm, "end": v(44.5, -37.57) * mm});
            skLineSegment(sketch, "E408", {"start": v(51.74, -37.57) * mm, "end": v(46.03, -37.57) * mm});
            skLineSegment(sketch, "E409", {"start": v(46.03, -37.57) * mm, "end": v(46.03, -27.07) * mm});
            skLineSegment(sketch, "E410", {"start": v(46.03, -27.07) * mm, "end": v(51.74, -27.07) * mm});
            skLineSegment(sketch, "E411", {"start": v(51.74, -27.07) * mm, "end": v(51.74, -37.57) * mm});
            skLineSegment(sketch, "E412", {"start": v(37.25, -49.55) * mm, "end": v(31.53, -49.55) * mm});
            skLineSegment(sketch, "E413", {"start": v(31.53, -49.55) * mm, "end": v(31.53, -39.04) * mm});
            skLineSegment(sketch, "E414", {"start": v(31.53, -39.04) * mm, "end": v(37.25, -39.04) * mm});
            skLineSegment(sketch, "E415", {"start": v(37.25, -39.04) * mm, "end": v(37.25, -49.55) * mm});
            skLineSegment(sketch, "E416", {"start": v(44.5, -49.55) * mm, "end": v(38.78, -49.55) * mm});
            skLineSegment(sketch, "E417", {"start": v(38.78, -49.55) * mm, "end": v(38.78, -39.04) * mm});
            skLineSegment(sketch, "E418", {"start": v(38.78, -39.04) * mm, "end": v(44.5, -39.04) * mm});
            skLineSegment(sketch, "E419", {"start": v(44.5, -39.04) * mm, "end": v(44.5, -49.55) * mm});
            skLineSegment(sketch, "E420", {"start": v(51.74, -49.55) * mm, "end": v(46.03, -49.55) * mm});
            skLineSegment(sketch, "E421", {"start": v(46.03, -49.55) * mm, "end": v(46.03, -39.04) * mm});
            skLineSegment(sketch, "E422", {"start": v(46.03, -39.04) * mm, "end": v(51.74, -39.04) * mm});
            skLineSegment(sketch, "E423", {"start": v(51.74, -39.04) * mm, "end": v(51.74, -49.55) * mm});
            skLineSegment(sketch, "E424", {"start": v(51.74, -105.44) * mm, "end": v(31.53, -105.44) * mm});
            skLineSegment(sketch, "E425", {"start": v(31.53, -105.44) * mm, "end": v(31.53, -81.98) * mm});
            skLineSegment(sketch, "E426", {"start": v(31.53, -81.98) * mm, "end": v(51.74, -81.98) * mm});
            skLineSegment(sketch, "E427", {"start": v(51.74, -81.98) * mm, "end": v(51.74, -105.44) * mm});
            skLineSegment(sketch, "E428", {"start": v(51.74, -132.83) * mm, "end": v(31.53, -132.83) * mm});
            skLineSegment(sketch, "E429", {"start": v(31.53, -132.83) * mm, "end": v(31.53, -109.38) * mm});
            skLineSegment(sketch, "E430", {"start": v(31.53, -109.38) * mm, "end": v(51.74, -109.38) * mm});
            skLineSegment(sketch, "E431", {"start": v(51.74, -109.38) * mm, "end": v(51.74, -132.83) * mm});
            skLineSegment(sketch, "E432", {"start": v(81.38, -37.57) * mm, "end": v(87.1, -37.57) * mm});
            skLineSegment(sketch, "E433", {"start": v(87.1, -37.57) * mm, "end": v(87.1, -27.07) * mm});
            skLineSegment(sketch, "E434", {"start": v(87.1, -27.07) * mm, "end": v(81.38, -27.07) * mm});
            skLineSegment(sketch, "E435", {"start": v(81.38, -27.07) * mm, "end": v(81.38, -37.57) * mm});
            skLineSegment(sketch, "E436", {"start": v(74.13, -37.57) * mm, "end": v(79.85, -37.57) * mm});
            skLineSegment(sketch, "E437", {"start": v(79.85, -37.57) * mm, "end": v(79.85, -27.07) * mm});
            skLineSegment(sketch, "E438", {"start": v(79.85, -27.07) * mm, "end": v(74.13, -27.07) * mm});
            skLineSegment(sketch, "E439", {"start": v(74.13, -27.07) * mm, "end": v(74.13, -37.57) * mm});
            skLineSegment(sketch, "E440", {"start": v(66.88, -37.57) * mm, "end": v(72.6, -37.57) * mm});
            skLineSegment(sketch, "E441", {"start": v(72.6, -37.57) * mm, "end": v(72.6, -27.07) * mm});
            skLineSegment(sketch, "E442", {"start": v(72.6, -27.07) * mm, "end": v(66.88, -27.07) * mm});
            skLineSegment(sketch, "E443", {"start": v(66.88, -27.07) * mm, "end": v(66.88, -37.57) * mm});
            skLineSegment(sketch, "E444", {"start": v(81.38, -49.55) * mm, "end": v(87.1, -49.55) * mm});
            skLineSegment(sketch, "E445", {"start": v(87.1, -49.55) * mm, "end": v(87.1, -39.04) * mm});
            skLineSegment(sketch, "E446", {"start": v(87.1, -39.04) * mm, "end": v(81.38, -39.04) * mm});
            skLineSegment(sketch, "E447", {"start": v(81.38, -39.04) * mm, "end": v(81.38, -49.55) * mm});
            skLineSegment(sketch, "E448", {"start": v(74.13, -49.55) * mm, "end": v(79.85, -49.55) * mm});
            skLineSegment(sketch, "E449", {"start": v(79.85, -49.55) * mm, "end": v(79.85, -39.04) * mm});
            skLineSegment(sketch, "E450", {"start": v(79.85, -39.04) * mm, "end": v(74.13, -39.04) * mm});
            skLineSegment(sketch, "E451", {"start": v(74.13, -39.04) * mm, "end": v(74.13, -49.55) * mm});
            skLineSegment(sketch, "E452", {"start": v(66.88, -49.55) * mm, "end": v(72.6, -49.55) * mm});
            skLineSegment(sketch, "E453", {"start": v(72.6, -49.55) * mm, "end": v(72.6, -39.04) * mm});
            skLineSegment(sketch, "E454", {"start": v(72.6, -39.04) * mm, "end": v(66.88, -39.04) * mm});
            skLineSegment(sketch, "E455", {"start": v(66.88, -39.04) * mm, "end": v(66.88, -49.55) * mm});
            skLineSegment(sketch, "E456", {"start": v(66.88, -105.44) * mm, "end": v(87.1, -105.44) * mm});
            skLineSegment(sketch, "E457", {"start": v(87.1, -105.44) * mm, "end": v(87.1, -81.98) * mm});
            skLineSegment(sketch, "E458", {"start": v(87.1, -81.98) * mm, "end": v(66.88, -81.98) * mm});
            skLineSegment(sketch, "E459", {"start": v(66.88, -81.98) * mm, "end": v(66.88, -105.44) * mm});
            skLineSegment(sketch, "E460", {"start": v(66.88, -132.83) * mm, "end": v(87.1, -132.83) * mm});
            skLineSegment(sketch, "E461", {"start": v(87.1, -132.83) * mm, "end": v(87.1, -109.38) * mm});
            skLineSegment(sketch, "E462", {"start": v(87.1, -109.38) * mm, "end": v(66.88, -109.38) * mm});
            skLineSegment(sketch, "E463", {"start": v(66.88, -109.38) * mm, "end": v(66.88, -132.83) * mm});
            skLineSegment(sketch, "E464", {"start": v(66.88, -78.04) * mm, "end": v(87.1, -78.04) * mm});
            skLineSegment(sketch, "E465", {"start": v(87.1, -78.04) * mm, "end": v(87.1, -54.59) * mm});
            skLineSegment(sketch, "E466", {"start": v(87.1, -54.59) * mm, "end": v(66.88, -54.59) * mm});
            skLineSegment(sketch, "E467", {"start": v(66.88, -54.59) * mm, "end": v(66.88, -78.04) * mm});
            skLineSegment(sketch, "E468", {"start": v(60.29, -132.83) * mm, "end": v(58.34, -132.83) * mm});
            skLineSegment(sketch, "E469", {"start": v(58.34, -132.83) * mm, "end": v(58.34, -27.07) * mm});
            skLineSegment(sketch, "E470", {"start": v(58.34, -27.07) * mm, "end": v(60.29, -27.07) * mm});
            skLineSegment(sketch, "E471", {"start": v(60.29, -27.07) * mm, "end": v(60.29, -132.83) * mm});
            skLineSegment(sketch, "E472", {"start": v(31.53, -78.04) * mm, "end": v(51.75, -78.04) * mm});
            skLineSegment(sketch, "E473", {"start": v(51.75, -78.04) * mm, "end": v(51.75, -54.59) * mm});
            skLineSegment(sketch, "E474", {"start": v(51.75, -54.59) * mm, "end": v(31.53, -54.59) * mm});
            skLineSegment(sketch, "E475", {"start": v(31.53, -54.59) * mm, "end": v(31.53, -78.04) * mm});
            skLineSegment(sketch, "E476", {"start": v(77.31, -25.48) * mm, "end": v(41.31, -25.48) * mm});
            skLineSegment(sketch, "E477", {"start": v(41.31, -25.48) * mm, "end": v(41.31, -21.48) * mm});
            skLineSegment(sketch, "E478", {"start": v(41.31, -21.48) * mm, "end": v(77.31, -21.48) * mm});
            skLineSegment(sketch, "E479", {"start": v(77.31, -21.48) * mm, "end": v(77.31, -25.48) * mm});
            skLineSegment(sketch, "E480", {"start": v(167.47, 6.32) * mm, "end": v(125.47, 6.32) * mm});
            skLineSegment(sketch, "E481", {"start": v(125.47, 6.32) * mm, "end": v(125.47, -35.68) * mm});
            skLineSegment(sketch, "E482", {"start": v(125.47, -35.68) * mm, "end": v(167.47, -35.68) * mm});
            skLineSegment(sketch, "E483", {"start": v(167.47, -35.68) * mm, "end": v(167.47, 6.32) * mm});
            skLineSegment(sketch, "E484", {"start": v(165, 107.66) * mm, "end": v(162.87, 109.8) * mm});
            skLineSegment(sketch, "E485", {"start": v(162.87, 109.8) * mm, "end": v(165, 111.93) * mm});
            skLineSegment(sketch, "E486", {"start": v(165, 111.93) * mm, "end": v(162.88, 114.06) * mm});
            skLineSegment(sketch, "E487", {"start": v(162.88, 114.06) * mm, "end": v(160.75, 111.92) * mm});
            skLineSegment(sketch, "E488", {"start": v(160.75, 111.92) * mm, "end": v(158.6, 114.06) * mm});
            skLineSegment(sketch, "E489", {"start": v(158.6, 114.06) * mm, "end": v(156.49, 111.93) * mm});
            skLineSegment(sketch, "E490", {"start": v(156.49, 111.93) * mm, "end": v(158.62, 109.8) * mm});
            skLineSegment(sketch, "E491", {"start": v(158.62, 109.8) * mm, "end": v(156.49, 107.66) * mm});
            skLineSegment(sketch, "E492", {"start": v(156.49, 107.66) * mm, "end": v(158.6, 105.54) * mm});
            skLineSegment(sketch, "E493", {"start": v(158.6, 105.54) * mm, "end": v(160.75, 107.68) * mm});
            skLineSegment(sketch, "E494", {"start": v(160.75, 107.68) * mm, "end": v(162.88, 105.54) * mm});
            skLineSegment(sketch, "E495", {"start": v(162.88, 105.54) * mm, "end": v(165, 107.66) * mm});
            skLineSegment(sketch, "E496", {"start": v(172.74, 97.8) * mm, "end": v(148.74, 97.8) * mm});
            skLineSegment(sketch, "E497", {"start": v(148.74, 97.8) * mm, "end": v(148.74, 121.8) * mm});
            skLineSegment(sketch, "E498", {"start": v(148.74, 121.8) * mm, "end": v(172.74, 121.8) * mm});
            skLineSegment(sketch, "E499", {"start": v(172.74, 121.8) * mm, "end": v(172.74, 97.8) * mm});
            skLineSegment(sketch, "E500", {"start": v(163.63, -86.06) * mm, "end": v(158.44, -86.06) * mm});
            skArc(sketch, "E501", {"start": v(158.44, -86.06) * mm, "mid": v(155.72, -81.96) * mm, "end": v(151.98, -78.77) * mm});
            skArc(sketch, "E502", {"start": v(151.98, -78.77) * mm, "mid": v(147.5, -76.75) * mm, "end": v(142.63, -76.06) * mm});
            skArc(sketch, "E503", {"start": v(142.63, -76.06) * mm, "mid": v(140.17, -76.23) * mm, "end": v(137.75, -76.75) * mm});
            skArc(sketch, "E504", {"start": v(137.75, -76.75) * mm, "mid": v(134.33, -78.15) * mm, "end": v(131.29, -80.23) * mm});
            skArc(sketch, "E505", {"start": v(131.29, -80.23) * mm, "mid": v(128.74, -82.91) * mm, "end": v(126.81, -86.06) * mm});
            skLineSegment(sketch, "E506", {"start": v(126.81, -86.06) * mm, "end": v(121.63, -86.06) * mm});
            skLineSegment(sketch, "E507", {"start": v(121.63, -86.06) * mm, "end": v(121.63, -101.06) * mm});
            skLineSegment(sketch, "E508", {"start": v(121.63, -101.06) * mm, "end": v(126.81, -101.06) * mm});
            skArc(sketch, "E509", {"start": v(126.81, -101.06) * mm, "mid": v(129.53, -105.16) * mm, "end": v(133.27, -108.35) * mm});
            skArc(sketch, "E510", {"start": v(133.27, -108.35) * mm, "mid": v(137.75, -110.37) * mm, "end": v(142.63, -111.06) * mm});
            skArc(sketch, "E511", {"start": v(142.63, -111.06) * mm, "mid": v(145.09, -110.89) * mm, "end": v(147.5, -110.37) * mm});
            skArc(sketch, "E512", {"start": v(147.5, -110.37) * mm, "mid": v(150.92, -108.98) * mm, "end": v(153.96, -106.89) * mm});
            skArc(sketch, "E513", {"start": v(153.96, -106.89) * mm, "mid": v(156.5, -104.21) * mm, "end": v(158.44, -101.06) * mm});
            skLineSegment(sketch, "E514", {"start": v(158.44, -101.06) * mm, "end": v(163.63, -101.06) * mm});
            skLineSegment(sketch, "E515", {"start": v(163.63, -101.06) * mm, "end": v(163.63, -86.06) * mm});
            skLineSegment(sketch, "E516", {"start": v(164.47, 8.27) * mm, "end": v(128.47, 8.27) * mm});
            skLineSegment(sketch, "E517", {"start": v(128.47, 8.27) * mm, "end": v(128.47, 12.27) * mm});
            skLineSegment(sketch, "E518", {"start": v(128.47, 12.27) * mm, "end": v(164.47, 12.27) * mm});
            skLineSegment(sketch, "E519", {"start": v(164.47, 12.27) * mm, "end": v(164.47, 8.27) * mm});
            skLineSegment(sketch, "E520", {"start": v(178.74, 132.75) * mm, "end": v(142.75, 132.75) * mm});
            skLineSegment(sketch, "E521", {"start": v(142.75, 132.75) * mm, "end": v(142.75, 136.75) * mm});
            skLineSegment(sketch, "E522", {"start": v(142.75, 136.75) * mm, "end": v(178.74, 136.75) * mm});
            skLineSegment(sketch, "E523", {"start": v(178.74, 136.75) * mm, "end": v(178.74, 132.75) * mm});
            skLineSegment(sketch, "E524", {"start": v(-39.56, -1.8) * mm, "end": v(-120.56, -1.8) * mm});
            skLineSegment(sketch, "E525", {"start": v(-120.56, -1.8) * mm, "end": v(-201.56, -1.8) * mm});
            skLineSegment(sketch, "E526", {"start": v(-120.56, 4.12) * mm, "end": v(-120.56, -1.8) * mm});
            skLineSegment(sketch, "E527", {"start": v(-120.56, -1.8) * mm, "end": v(-120.56, -7.73) * mm});
            skLineSegment(sketch, "E528", {"start": v(-129.71, 5.95) * mm, "end": v(-129.71, 20.95) * mm});
            skLineSegment(sketch, "E529", {"start": v(-129.71, 20.95) * mm, "end": v(-132.71, 20.95) * mm});
            skLineSegment(sketch, "E530", {"start": v(-132.71, 20.95) * mm, "end": v(-132.71, 35.95) * mm});
            skLineSegment(sketch, "E531", {"start": v(-132.71, 35.95) * mm, "end": v(-129.71, 35.95) * mm});
            skLineSegment(sketch, "E532", {"start": v(-129.71, 35.95) * mm, "end": v(-129.71, 50.95) * mm});
            skLineSegment(sketch, "E533", {"start": v(-129.71, 50.95) * mm, "end": v(-132.71, 50.95) * mm});
            skLineSegment(sketch, "E534", {"start": v(-132.71, 50.95) * mm, "end": v(-132.71, 65.95) * mm});
            skLineSegment(sketch, "E535", {"start": v(-132.71, 65.95) * mm, "end": v(-129.71, 65.95) * mm});
            skLineSegment(sketch, "E536", {"start": v(-129.71, 65.95) * mm, "end": v(-129.71, 80.95) * mm});
            skLineSegment(sketch, "E537", {"start": v(-129.71, 80.95) * mm, "end": v(-132.71, 80.95) * mm});
            skLineSegment(sketch, "E538", {"start": v(-132.71, 80.95) * mm, "end": v(-132.71, 95.95) * mm});
            skLineSegment(sketch, "E539", {"start": v(-132.71, 95.95) * mm, "end": v(-129.71, 95.95) * mm});
            skLineSegment(sketch, "E540", {"start": v(-129.71, 95.95) * mm, "end": v(-129.71, 110.95) * mm});
            skLineSegment(sketch, "E541", {"start": v(-129.71, 110.95) * mm, "end": v(-132.71, 110.95) * mm});
            skLineSegment(sketch, "E542", {"start": v(-132.71, 110.95) * mm, "end": v(-132.71, 125.95) * mm});
            skLineSegment(sketch, "E543", {"start": v(-132.71, 125.95) * mm, "end": v(-129.71, 125.95) * mm});
            skLineSegment(sketch, "E544", {"start": v(-129.71, 125.95) * mm, "end": v(-129.71, 140.95) * mm});
            skLineSegment(sketch, "E545", {"start": v(-63.71, 140.95) * mm, "end": v(-63.71, 125.95) * mm});
            skLineSegment(sketch, "E546", {"start": v(-63.71, 125.95) * mm, "end": v(-60.71, 125.95) * mm});
            skLineSegment(sketch, "E547", {"start": v(-60.71, 125.95) * mm, "end": v(-60.71, 110.95) * mm});
            skLineSegment(sketch, "E548", {"start": v(-60.71, 110.95) * mm, "end": v(-63.71, 110.95) * mm});
            skLineSegment(sketch, "E549", {"start": v(-63.71, 110.95) * mm, "end": v(-63.71, 95.95) * mm});
            skLineSegment(sketch, "E550", {"start": v(-63.71, 95.95) * mm, "end": v(-60.71, 95.95) * mm});
            skLineSegment(sketch, "E551", {"start": v(-60.71, 95.95) * mm, "end": v(-60.71, 80.95) * mm});
            skLineSegment(sketch, "E552", {"start": v(-60.71, 80.95) * mm, "end": v(-63.71, 80.95) * mm});
            skLineSegment(sketch, "E553", {"start": v(-63.71, 80.95) * mm, "end": v(-63.71, 65.95) * mm});
            skLineSegment(sketch, "E554", {"start": v(-63.71, 65.95) * mm, "end": v(-60.71, 65.95) * mm});
            skLineSegment(sketch, "E555", {"start": v(-60.71, 65.95) * mm, "end": v(-60.71, 50.95) * mm});
            skLineSegment(sketch, "E556", {"start": v(-60.71, 50.95) * mm, "end": v(-63.71, 50.95) * mm});
            skLineSegment(sketch, "E557", {"start": v(-63.71, 50.95) * mm, "end": v(-63.71, 35.95) * mm});
            skLineSegment(sketch, "E558", {"start": v(-63.71, 35.95) * mm, "end": v(-60.71, 35.95) * mm});
            skLineSegment(sketch, "E559", {"start": v(-60.71, 35.95) * mm, "end": v(-60.71, 20.95) * mm});
            skLineSegment(sketch, "E560", {"start": v(-60.71, 20.95) * mm, "end": v(-63.71, 20.95) * mm});
            skLineSegment(sketch, "E561", {"start": v(-63.71, 20.95) * mm, "end": v(-63.71, 5.95) * mm});
            skLineSegment(sketch, "E562", {"start": v(8.29, 5.95) * mm, "end": v(8.29, 20.95) * mm});
            skLineSegment(sketch, "E563", {"start": v(8.29, 20.95) * mm, "end": v(5.29, 20.95) * mm});
            skLineSegment(sketch, "E564", {"start": v(5.29, 20.95) * mm, "end": v(5.29, 35.95) * mm});
            skLineSegment(sketch, "E565", {"start": v(5.29, 35.95) * mm, "end": v(8.29, 35.95) * mm});
            skLineSegment(sketch, "E566", {"start": v(8.29, 35.95) * mm, "end": v(8.29, 50.95) * mm});
            skLineSegment(sketch, "E567", {"start": v(8.29, 50.95) * mm, "end": v(5.29, 50.95) * mm});
            skLineSegment(sketch, "E568", {"start": v(5.29, 50.95) * mm, "end": v(5.29, 65.95) * mm});
            skLineSegment(sketch, "E569", {"start": v(5.29, 65.95) * mm, "end": v(8.29, 65.95) * mm});
            skLineSegment(sketch, "E570", {"start": v(8.29, 65.95) * mm, "end": v(8.29, 80.95) * mm});
            skLineSegment(sketch, "E571", {"start": v(8.29, 80.95) * mm, "end": v(5.29, 80.95) * mm});
            skLineSegment(sketch, "E572", {"start": v(5.29, 80.95) * mm, "end": v(5.29, 95.95) * mm});
            skLineSegment(sketch, "E573", {"start": v(5.29, 95.95) * mm, "end": v(8.29, 95.95) * mm});
            skLineSegment(sketch, "E574", {"start": v(8.29, 95.95) * mm, "end": v(8.29, 110.95) * mm});
            skLineSegment(sketch, "E575", {"start": v(8.29, 110.95) * mm, "end": v(5.29, 110.95) * mm});
            skLineSegment(sketch, "E576", {"start": v(5.29, 110.95) * mm, "end": v(5.29, 125.95) * mm});
            skLineSegment(sketch, "E577", {"start": v(5.29, 125.95) * mm, "end": v(8.29, 125.95) * mm});
            skLineSegment(sketch, "E578", {"start": v(8.29, 125.95) * mm, "end": v(8.29, 140.95) * mm});
            skLineSegment(sketch, "E579", {"start": v(150.73, -16.82) * mm, "end": v(148.6, -14.68) * mm});
            skLineSegment(sketch, "E580", {"start": v(148.6, -14.68) * mm, "end": v(150.73, -12.55) * mm});
            skLineSegment(sketch, "E581", {"start": v(150.73, -12.55) * mm, "end": v(148.6, -10.42) * mm});
            skLineSegment(sketch, "E582", {"start": v(148.6, -10.42) * mm, "end": v(146.47, -12.56) * mm});
            skLineSegment(sketch, "E583", {"start": v(146.47, -12.56) * mm, "end": v(144.34, -10.42) * mm});
            skLineSegment(sketch, "E584", {"start": v(144.34, -10.42) * mm, "end": v(142.22, -12.55) * mm});
            skLineSegment(sketch, "E585", {"start": v(142.22, -12.55) * mm, "end": v(144.35, -14.68) * mm});
            skLineSegment(sketch, "E586", {"start": v(144.35, -14.68) * mm, "end": v(142.22, -16.82) * mm});
            skLineSegment(sketch, "E587", {"start": v(142.22, -16.82) * mm, "end": v(144.34, -18.94) * mm});
            skLineSegment(sketch, "E588", {"start": v(144.34, -18.94) * mm, "end": v(146.47, -16.8) * mm});
            skLineSegment(sketch, "E589", {"start": v(146.47, -16.8) * mm, "end": v(148.6, -18.94) * mm});
            skLineSegment(sketch, "E590", {"start": v(148.6, -18.94) * mm, "end": v(150.73, -16.82) * mm});
            skLineSegment(sketch, "E591", {"start": v(117.4, -93.56) * mm, "end": v(111.4, -93.56) * mm});
            skLineSegment(sketch, "E592", {"start": v(142.63, -70.69) * mm, "end": v(142.63, -64.69) * mm});
            skLineSegment(sketch, "E593", {"start": v(86.4, 117.12) * mm, "end": v(82.82, 117.12) * mm});
            skLineSegment(sketch, "E594.top", {"start": v(118.32, 27.57) * mm, "end": v(190.28, 27.57) * mm});
            skLineSegment(sketch, "E594.left", {"start": v(118.32, 39.57) * mm, "end": v(118.32, 27.57) * mm});
            skSolve(sketch);
        }
        {
            var Q0;
            {var subQ2=sQuery(id+"F0.wireOp",EDGE,"E134");Q0=makeQuery(id+"F0.imprint","IMPRINT",FACE,{"disambiguationData":[TD([[makeQuery(id+"F0.imprint","IMPRINT",EDGE,{"derivedFrom":subQ2}),1.0]])]});}
            var Q1;
            Q1=makeQuery(id+"F0.imprint","IMPRINT",FACE,{"disambiguationData":[TD([[makeQuery(id+"F0.imprint","IMPRINT",EDGE,{"derivedFrom":sQuery(id+"F0.wireOp",EDGE,"E160")}),1.0]])]});
            var Q2;
            Q2=makeQuery(id+"F0.imprint","IMPRINT",FACE,{"disambiguationData":[TD([[makeQuery(id+"F0.imprint","IMPRINT",EDGE,{"derivedFrom":sQuery(id+"F0.wireOp",EDGE,"E89")}),1.0]])]});
            var Q3;
            {var subQ0=sQuery(id+"F0.wireOp",EDGE,"E95");Q3=makeQuery(id+"F0.imprint","IMPRINT",FACE,{"disambiguationData":[TD([[makeQuery(id+"F0.imprint","IMPRINT",EDGE,{"derivedFrom":subQ0}),-1.0]])]});}
            var Q4;
            Q4=makeQuery(id+"F0.imprint","IMPRINT",FACE,{"disambiguationData":[TD([[makeQuery(id+"F0.imprint","IMPRINT",EDGE,{"derivedFrom":sQuery(id+"F0.wireOp",EDGE,"E111")}),1.0]])]});
            var Q5;
            Q5=makeQuery(id+"F0.imprint","IMPRINT",FACE,{"disambiguationData":[TD([[makeQuery(id+"F0.imprint","IMPRINT",EDGE,{"derivedFrom":sQuery(id+"F0.wireOp",EDGE,"E108")}),1.0]])]});
            var Q6;
            Q6=makeQuery(id+"F0.imprint","IMPRINT",FACE,{"disambiguationData":[TD([[makeQuery(id+"F0.imprint","IMPRINT",EDGE,{"derivedFrom":sQuery(id+"F0.wireOp",EDGE,"E104")}),-1.0]])]});
            var Q7;
            {var subQ0=sQuery(id+"F0.wireOp",EDGE,"E75");Q7=makeQuery(id+"F0.imprint","IMPRINT",FACE,{"disambiguationData":[TD([[makeQuery(id+"F0.imprint","IMPRINT",EDGE,{"derivedFrom":subQ0}),-1.0]])]});}
            var Q8;
            {var subQ0=sQuery(id+"F0.wireOp",EDGE,"E81");Q8=makeQuery(id+"F0.imprint","IMPRINT",FACE,{"disambiguationData":[TD([[makeQuery(id+"F0.imprint","IMPRINT",EDGE,{"derivedFrom":subQ0}),-1.0]])]});}
            var Q9;
            Q9=makeQuery(id+"F0.imprint","IMPRINT",FACE,{"disambiguationData":[TD([[makeQuery(id+"F0.imprint","IMPRINT",EDGE,{"derivedFrom":sQuery(id+"F0.wireOp",EDGE,"E85")}),-1.0]])]});
            var Q10;
            Q10=makeQuery(id+"F0.imprint","IMPRINT",FACE,{"disambiguationData":[TD([[makeQuery(id+"F0.imprint","IMPRINT",EDGE,{"derivedFrom":sQuery(id+"F0.wireOp",EDGE,"E31")}),1.0]])]});
            var Q11;
            Q11=makeQuery(id+"F0.imprint","IMPRINT",FACE,{"disambiguationData":[TD([[makeQuery(id+"F0.imprint","IMPRINT",EDGE,{"derivedFrom":sQuery(id+"F0.wireOp",EDGE,"E4")}),-1.0]])]});
            var Q12;
            Q12=makeQuery(id+"F0.imprint","IMPRINT",FACE,{"disambiguationData":[TD([[makeQuery(id+"F0.imprint","IMPRINT",EDGE,{"derivedFrom":sQuery(id+"F0.wireOp",EDGE,"E16")}),-1.0]])]});
            var Q13;
            Q13=makeQuery(id+"F0.imprint","IMPRINT",FACE,{"disambiguationData":[TD([[makeQuery(id+"F0.imprint","IMPRINT",EDGE,{"derivedFrom":sQuery(id+"F0.wireOp",EDGE,"E51")}),1.0]])]});
            var Q14;
            Q14=makeQuery(id+"F0.imprint","IMPRINT",FACE,{"disambiguationData":[TD([[makeQuery(id+"F0.imprint","IMPRINT",EDGE,{"derivedFrom":sQuery(id+"F0.wireOp",EDGE,"E61")}),1.0]])]});
            extrude(context, id + "F1", {"entities" : qUnion([Q0, Q1, Q2, Q3, Q4, Q5, Q6, Q7, Q8, Q9, Q10, Q11, Q12, Q13, Q14]), "depth" : 3 * mm});
        }
        {
            var Q0;
            Q0=makeQuery(id+"F0.imprint","IMPRINT",FACE,{"disambiguationData":[TD([[makeQuery(id+"F0.imprint","IMPRINT",EDGE,{"derivedFrom":sQuery(id+"F0.wireOp",EDGE,"E156")}),1.0]])]});
            var Q1;
            {var subQ2=sQuery(id+"F0.wireOp",EDGE,"E116");Q1=makeQuery(id+"F0.imprint","IMPRINT",FACE,{"disambiguationData":[TD([[makeQuery(id+"F0.imprint","IMPRINT",EDGE,{"derivedFrom":subQ2}),1.0]])]});}
            var Q2;
            Q2=makeQuery(id+"F0.imprint","IMPRINT",FACE,{"disambiguationData":[TD([[makeQuery(id+"F0.imprint","IMPRINT",EDGE,{"derivedFrom":sQuery(id+"F0.wireOp",EDGE,"E92")}),-1.0]])]});
            var Q3;
            Q3=makeQuery(id+"F0.imprint","IMPRINT",FACE,{"disambiguationData":[TD([[makeQuery(id+"F0.imprint","IMPRINT",EDGE,{"derivedFrom":sQuery(id+"F0.wireOp",EDGE,"E99")}),-1.0]])]});
            var Q4;
            Q4=makeQuery(id+"F0.imprint","IMPRINT",FACE,{"disambiguationData":[TD([[makeQuery(id+"F0.imprint","IMPRINT",EDGE,{"derivedFrom":sQuery(id+"F0.wireOp",EDGE,"E113")}),1.0]])]});
            var Q5;
            Q5=makeQuery(id+"F0.imprint","IMPRINT",FACE,{"disambiguationData":[TD([[makeQuery(id+"F0.imprint","IMPRINT",EDGE,{"derivedFrom":sQuery(id+"F0.wireOp",EDGE,"E109")}),1.0]])]});
            var Q6;
            Q6=makeQuery(id+"F0.imprint","IMPRINT",FACE,{"disambiguationData":[TD([[makeQuery(id+"F0.imprint","IMPRINT",EDGE,{"derivedFrom":sQuery(id+"F0.wireOp",EDGE,"E500")}),1.0]])]});
            var Q7;
            Q7=makeQuery(id+"F0.imprint","IMPRINT",FACE,{"disambiguationData":[TD([[makeQuery(id+"F0.imprint","IMPRINT",EDGE,{"derivedFrom":sQuery(id+"F0.wireOp",EDGE,"E480")}),1.0]])]});
            var Q8;
            Q8=makeQuery(id+"F0.imprint","IMPRINT",FACE,{"disambiguationData":[TD([[makeQuery(id+"F0.imprint","IMPRINT",EDGE,{"derivedFrom":sQuery(id+"F0.wireOp",EDGE,"E484")}),-1.0]])]});
            var Q9;
            {var subQ4=sQuery(id+"F0.wireOp",EDGE,"E72");Q9=makeQuery(id+"F0.imprint","IMPRINT",FACE,{"disambiguationData":[TD([[makeQuery(id+"F0.imprint","IMPRINT",EDGE,{"derivedFrom":subQ4}),-1.0]])]});}
            var Q10;
            {var subQ1=sQuery(id+"F0.wireOp",EDGE,"E78");var subQ5=makeQuery(id+"F0.imprint","IMPRINT",VERTEX,{"derivedFrom":subQ1});Q10=makeQuery(id+"F0.imprint","IMPRINT",FACE,{"disambiguationData":[TD([[makeQuery(id+"F0.imprint","IMPRINT",EDGE,{"disambiguationData":[TD([[subQ5,1.0]])],"derivedFrom":subQ1}),-1.0]])]});}
            var Q11;
            Q11=makeQuery(id+"F0.imprint","IMPRINT",FACE,{"disambiguationData":[TD([[makeQuery(id+"F0.imprint","IMPRINT",EDGE,{"derivedFrom":sQuery(id+"F0.wireOp",EDGE,"E82")}),-1.0]])]});
            extrude(context, id + "F2", {"entities" : qUnion([Q0, Q1, Q2, Q3, Q4, Q5, Q6, Q7, Q8, Q9, Q10, Q11]), "depth" : 3 * mm});
        }
        {
            var Q0;
            Q0=makeQuery(id+"F2.opExtrude","CAP_EDGE",EDGE,{"disambiguationData":[OSD([sQuery(id+"F0.wireOp",EDGE,"E508")])],"isStart":false});
            var Q1;
            Q1=makeQuery(id+"F2.opExtrude","CAP_EDGE",EDGE,{"disambiguationData":[OSD([sQuery(id+"F0.wireOp",EDGE,"E506")])],"isStart":false});
            var Q2;
            Q2=makeQuery(id+"F2.opExtrude","CAP_EDGE",EDGE,{"disambiguationData":[OSD([sQuery(id+"F0.wireOp",EDGE,"E514")])],"isStart":false});
            var Q3;
            Q3=makeQuery(id+"F2.opExtrude","CAP_EDGE",EDGE,{"disambiguationData":[OSD([sQuery(id+"F0.wireOp",EDGE,"E500")])],"isStart":false});
            chamfer(context, id + "F3", {"entities" : qUnion([Q0, Q1, Q2, Q3]), "chamferType" : ChamferType.TWO_OFFSETS, "width1" : 5 * mm, "oppositeDirection" : false, "width2" : .5 * mm, "tangentPropagation" : true});
        }
    });
